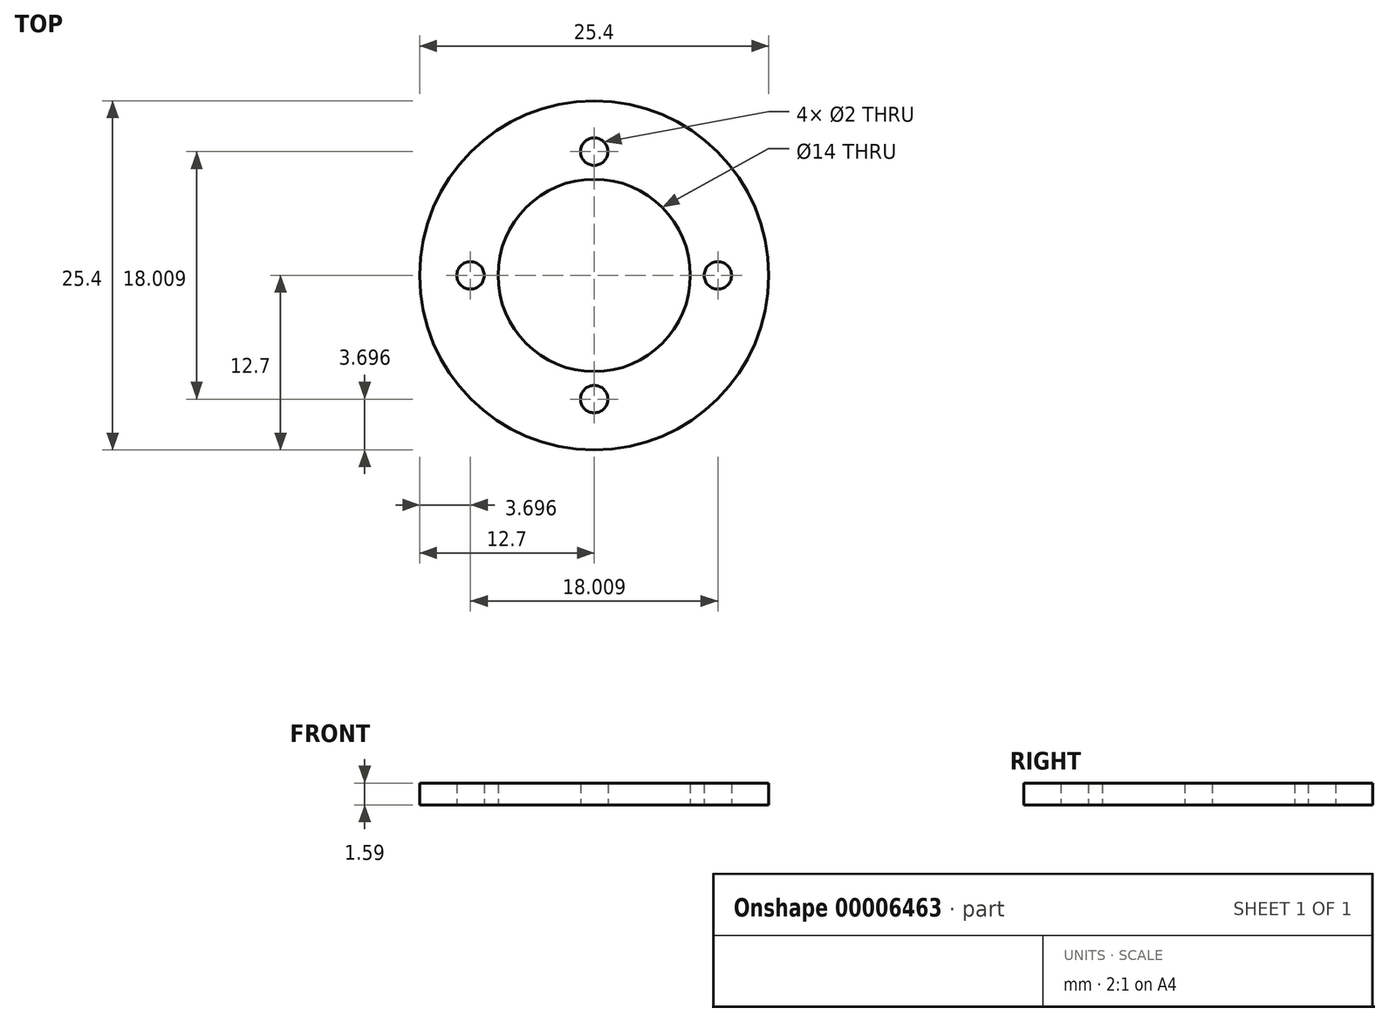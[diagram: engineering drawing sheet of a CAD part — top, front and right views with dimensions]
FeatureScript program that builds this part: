
annotation { "Feature Type Name" : "Feature", "Feature Type Description" : "" }
export const myFeature = defineFeature(function(context is Context, id is Id, definition is map)
    precondition{}
    {
        {
            var Q0;
            Q0=qCreatedBy(makeId("Top.planeOp"),FACE);
            var sketch = newSketch(context, id + "F0", { "sketchPlane" : qUnion([Q0])});
            skCircle(sketch, "E0", {"center": v(0, 0) * mm, "radius": 12.7 * mm});
            skCircle(sketch, "E1", {"center": v(0, 0) * mm, "radius": 9 * mm, "construction": true});
            skCircle(sketch, "E2", {"center": v(0, 9) * mm, "radius": 1 * mm});
            skCircle(sketch, "E3", {"center": v(9, 0) * mm, "radius": 1 * mm});
            skCircle(sketch, "E4", {"center": v(0, -9) * mm, "radius": 1 * mm});
            skCircle(sketch, "E5", {"center": v(-9, 0) * mm, "radius": 1 * mm});
            skCircle(sketch, "E6", {"center": v(0, 0) * mm, "radius": 7 * mm});
            skSolve(sketch);
        }
        {
            var Q0;
            Q0=makeQuery(id+"F0.imprint","IMPRINT",FACE,{"disambiguationData":[TD([[makeQuery(id+"F0.imprint","IMPRINT",EDGE,{"derivedFrom":sQuery(id+"F0.wireOp",EDGE,"E0")}),1.0]])]});
            extrude(context, id + "F1", {"entities" : qUnion([Q0]), "depth" : 1.59 * mm});
        }
    });
